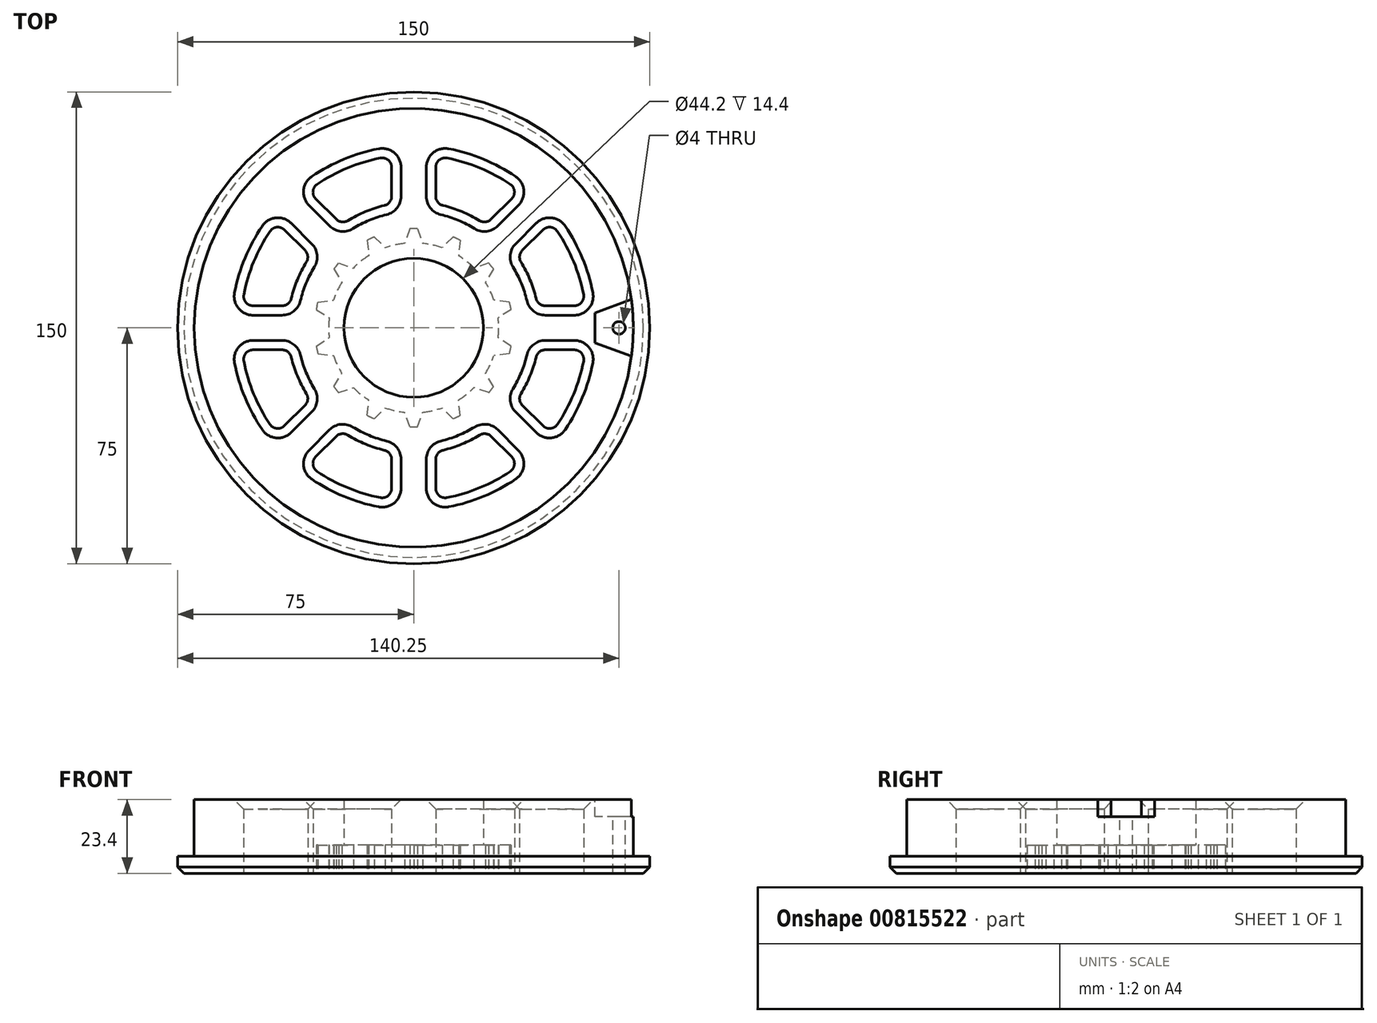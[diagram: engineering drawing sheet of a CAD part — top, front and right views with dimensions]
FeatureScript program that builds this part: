
annotation { "Feature Type Name" : "Feature", "Feature Type Description" : "" }
export const myFeature = defineFeature(function(context is Context, id is Id, definition is map)
    precondition{}
    {
        {
            var Q0;
            Q0=qCreatedBy(makeId("Top.planeOp"),FACE);
            var sketch = newSketch(context, id + "F0", { "sketchPlane" : qUnion([Q0])});
            skCircle(sketch, "E0", {"center": v(0, 0) * mm, "radius": 22.1 * mm});
            skCircle(sketch, "E1", {"center": v(0, 0) * mm, "radius": 75 * mm});
            skSolve(sketch);
        }
        {
            var Q0;
            Q0=qSketchRegion(id+"F0",true);
            extrude(context, id + "F1", {"entities" : qUnion([Q0]), "depth" : 23.4 * mm, "offsetDistance" : 25 * mm});
        }
        {
            var Q0;
            Q0=makeQuery(id+"F1.opExtrude","CAP_FACE",FACE,{"disambiguationData":[OSD([sQuery(id+"F0.wireOp",EDGE,"E0"),sQuery(id+"F0.wireOp",EDGE,"E1")])],"isStart":true});
            var sketch = newSketch(context, id + "F2", { "sketchPlane" : qUnion([Q0])});
            skCircle(sketch, "E2.0", {"center": v(0, 0) * mm, "radius": 22.1 * mm});
            skArc(sketch, "E3", {"start": v(2.9, -26.84) * mm, "mid": v(6, -26.32) * mm, "end": v(9.03, -25.44) * mm});
            skLineSegment(sketch, "E4", {"start": v(0, 0) * mm, "end": v(0, 59.3) * mm, "construction": true});
            skArc(sketch, "E5", {"start": v(0, -31.5) * mm, "mid": v(0.63, -31.5) * mm, "end": v(1.25, -31.48) * mm, "construction": true});
            skLineSegment(sketch, "E6", {"start": v(0, 31.5) * mm, "end": v(-1.25, 31.48) * mm});
            skLineSegment(sketch, "E7.MirrorCS", {"start": v(0, 31.5) * mm, "end": v(1.25, 31.48) * mm});
            skLineSegment(sketch, "E8", {"start": v(-1.25, 31.48) * mm, "end": v(-2.9, 26.84) * mm});
            skLineSegment(sketch, "E9", {"start": v(1.25, 31.48) * mm, "end": v(2.9, 26.84) * mm});
            skArc(sketch, "E10.1.0", {"start": v(0, -31.5) * mm, "mid": v(0.63, -31.5) * mm, "end": v(1.25, -31.48) * mm});
            skLineSegment(sketch, "E11.1.0", {"start": v(-12.53, 28.9) * mm, "end": v(-9.03, 25.44) * mm});
            skLineSegment(sketch, "E11.1.1", {"start": v(-14.78, 27.82) * mm, "end": v(-14.26, 22.93) * mm});
            skLineSegment(sketch, "E11.1.2", {"start": v(-13.67, 28.38) * mm, "end": v(-12.53, 28.9) * mm});
            skLineSegment(sketch, "E11.1.3", {"start": v(-13.67, 28.38) * mm, "end": v(-14.78, 27.82) * mm});
            skLineSegment(sketch, "E11.2.0", {"start": v(-23.83, 20.6) * mm, "end": v(-19.18, 19) * mm});
            skLineSegment(sketch, "E11.2.1", {"start": v(-25.39, 18.65) * mm, "end": v(-22.8, 14.47) * mm});
            skLineSegment(sketch, "E11.2.2", {"start": v(-24.63, 19.64) * mm, "end": v(-23.83, 20.6) * mm});
            skLineSegment(sketch, "E11.2.3", {"start": v(-24.63, 19.64) * mm, "end": v(-25.39, 18.65) * mm});
            skLineSegment(sketch, "E11.3.0", {"start": v(-30.4, 8.22) * mm, "end": v(-25.53, 8.8) * mm});
            skLineSegment(sketch, "E11.3.1", {"start": v(-30.96, 5.79) * mm, "end": v(-26.82, 3.15) * mm});
            skLineSegment(sketch, "E11.3.2", {"start": v(-30.71, 7) * mm, "end": v(-30.4, 8.22) * mm});
            skLineSegment(sketch, "E11.3.3", {"start": v(-30.71, 7) * mm, "end": v(-30.96, 5.79) * mm});
            skLineSegment(sketch, "E11.4.0", {"start": v(-30.96, -5.79) * mm, "end": v(-26.82, -3.15) * mm});
            skLineSegment(sketch, "E11.4.1", {"start": v(-30.4, -8.22) * mm, "end": v(-25.53, -8.8) * mm});
            skLineSegment(sketch, "E11.4.2", {"start": v(-30.71, -7) * mm, "end": v(-30.96, -5.79) * mm});
            skLineSegment(sketch, "E11.4.3", {"start": v(-30.71, -7) * mm, "end": v(-30.4, -8.22) * mm});
            skLineSegment(sketch, "E11.5.0", {"start": v(-25.39, -18.65) * mm, "end": v(-22.8, -14.47) * mm});
            skLineSegment(sketch, "E11.5.1", {"start": v(-23.83, -20.6) * mm, "end": v(-19.18, -19) * mm});
            skLineSegment(sketch, "E11.5.2", {"start": v(-24.63, -19.64) * mm, "end": v(-25.39, -18.65) * mm});
            skLineSegment(sketch, "E11.5.3", {"start": v(-24.63, -19.64) * mm, "end": v(-23.83, -20.6) * mm});
            skLineSegment(sketch, "E11.6.0", {"start": v(-14.78, -27.82) * mm, "end": v(-14.26, -22.93) * mm});
            skLineSegment(sketch, "E11.6.1", {"start": v(-12.53, -28.9) * mm, "end": v(-9.03, -25.44) * mm});
            skLineSegment(sketch, "E11.6.2", {"start": v(-13.67, -28.38) * mm, "end": v(-14.78, -27.82) * mm});
            skLineSegment(sketch, "E11.6.3", {"start": v(-13.67, -28.38) * mm, "end": v(-12.53, -28.9) * mm});
            skLineSegment(sketch, "E11.7.0", {"start": v(-1.25, -31.48) * mm, "end": v(-2.9, -26.84) * mm});
            skLineSegment(sketch, "E11.7.1", {"start": v(1.25, -31.48) * mm, "end": v(2.9, -26.84) * mm});
            skLineSegment(sketch, "E11.7.2", {"start": v(0, -31.5) * mm, "end": v(-1.25, -31.48) * mm});
            skLineSegment(sketch, "E11.7.3", {"start": v(0, -31.5) * mm, "end": v(1.25, -31.48) * mm});
            skLineSegment(sketch, "E11.8.0", {"start": v(12.53, -28.9) * mm, "end": v(9.03, -25.44) * mm});
            skLineSegment(sketch, "E11.8.1", {"start": v(14.78, -27.82) * mm, "end": v(14.26, -22.93) * mm});
            skLineSegment(sketch, "E11.8.2", {"start": v(13.67, -28.38) * mm, "end": v(12.53, -28.9) * mm});
            skLineSegment(sketch, "E11.8.3", {"start": v(13.67, -28.38) * mm, "end": v(14.78, -27.82) * mm});
            skLineSegment(sketch, "E11.9.0", {"start": v(23.83, -20.6) * mm, "end": v(19.18, -19) * mm});
            skLineSegment(sketch, "E11.9.1", {"start": v(25.39, -18.65) * mm, "end": v(22.8, -14.47) * mm});
            skLineSegment(sketch, "E11.9.2", {"start": v(24.63, -19.64) * mm, "end": v(23.83, -20.6) * mm});
            skLineSegment(sketch, "E11.9.3", {"start": v(24.63, -19.64) * mm, "end": v(25.39, -18.65) * mm});
            skLineSegment(sketch, "E11.10.0", {"start": v(30.4, -8.22) * mm, "end": v(25.53, -8.8) * mm});
            skLineSegment(sketch, "E11.10.1", {"start": v(30.96, -5.79) * mm, "end": v(26.82, -3.15) * mm});
            skLineSegment(sketch, "E11.10.2", {"start": v(30.71, -7) * mm, "end": v(30.4, -8.22) * mm});
            skLineSegment(sketch, "E11.10.3", {"start": v(30.71, -7) * mm, "end": v(30.96, -5.79) * mm});
            skLineSegment(sketch, "E11.11.0", {"start": v(30.96, 5.79) * mm, "end": v(26.82, 3.15) * mm});
            skLineSegment(sketch, "E11.11.1", {"start": v(30.4, 8.22) * mm, "end": v(25.53, 8.8) * mm});
            skLineSegment(sketch, "E11.11.2", {"start": v(30.71, 7) * mm, "end": v(30.96, 5.79) * mm});
            skLineSegment(sketch, "E11.11.3", {"start": v(30.71, 7) * mm, "end": v(30.4, 8.22) * mm});
            skLineSegment(sketch, "E11.12.0", {"start": v(25.39, 18.65) * mm, "end": v(22.8, 14.47) * mm});
            skLineSegment(sketch, "E11.12.1", {"start": v(23.83, 20.6) * mm, "end": v(19.18, 19) * mm});
            skLineSegment(sketch, "E11.12.2", {"start": v(24.63, 19.64) * mm, "end": v(25.39, 18.65) * mm});
            skLineSegment(sketch, "E11.12.3", {"start": v(24.63, 19.64) * mm, "end": v(23.83, 20.6) * mm});
            skLineSegment(sketch, "E11.13.0", {"start": v(14.78, 27.82) * mm, "end": v(14.26, 22.93) * mm});
            skLineSegment(sketch, "E11.13.1", {"start": v(12.53, 28.9) * mm, "end": v(9.03, 25.44) * mm});
            skLineSegment(sketch, "E11.13.2", {"start": v(13.67, 28.38) * mm, "end": v(14.78, 27.82) * mm});
            skLineSegment(sketch, "E11.13.3", {"start": v(13.67, 28.38) * mm, "end": v(12.53, 28.9) * mm});
            skArc(sketch, "E12.trimOffspring", {"start": v(-2.9, 26.84) * mm, "mid": v(-6, 26.32) * mm, "end": v(-9.03, 25.44) * mm, "construction": true});
            skPoint(sketch, "E13.start.orphan", {"position": v(0, 27) * mm});
            skArc(sketch, "E14.trimOffspring", {"start": v(-2.9, 26.84) * mm, "mid": v(-6, 26.32) * mm, "end": v(-9.03, 25.44) * mm});
            skArc(sketch, "E15.trimOffspring", {"start": v(-12.53, 28.9) * mm, "mid": v(-13.67, 28.38) * mm, "end": v(-14.78, 27.82) * mm, "construction": true});
            skArc(sketch, "E16.trimOffspring", {"start": v(-12.53, 28.9) * mm, "mid": v(-13.67, 28.38) * mm, "end": v(-14.78, 27.82) * mm});
            skArc(sketch, "E17.trimOffspring", {"start": v(1.25, 31.48) * mm, "mid": v(0, 31.5) * mm, "end": v(-1.25, 31.48) * mm, "construction": true});
            skArc(sketch, "E18.trimOffspring", {"start": v(1.25, 31.48) * mm, "mid": v(0, 31.5) * mm, "end": v(-1.25, 31.48) * mm});
            skArc(sketch, "E19.trimOffspring", {"start": v(9.03, 25.44) * mm, "mid": v(6, 26.32) * mm, "end": v(2.9, 26.84) * mm});
            skArc(sketch, "E20.trimOffspring", {"start": v(14.78, 27.82) * mm, "mid": v(13.67, 28.38) * mm, "end": v(12.53, 28.9) * mm, "construction": true});
            skArc(sketch, "E21.trimOffspring", {"start": v(14.78, 27.82) * mm, "mid": v(13.67, 28.38) * mm, "end": v(12.53, 28.9) * mm});
            skArc(sketch, "E22.trimOffspring", {"start": v(25.39, 18.65) * mm, "mid": v(24.63, 19.64) * mm, "end": v(23.83, 20.6) * mm, "construction": true});
            skArc(sketch, "E23.trimOffspring", {"start": v(19.18, 19) * mm, "mid": v(16.83, 21.1) * mm, "end": v(14.26, 22.93) * mm});
            skArc(sketch, "E24.trimOffspring", {"start": v(25.39, 18.65) * mm, "mid": v(24.63, 19.64) * mm, "end": v(23.83, 20.6) * mm});
            skArc(sketch, "E25.trimOffspring", {"start": v(25.53, 8.8) * mm, "mid": v(24.33, 11.71) * mm, "end": v(22.8, 14.47) * mm});
            skArc(sketch, "E26.trimOffspring", {"start": v(30.96, 5.79) * mm, "mid": v(30.71, 7) * mm, "end": v(30.4, 8.22) * mm, "construction": true});
            skArc(sketch, "E27.trimOffspring", {"start": v(30.96, 5.79) * mm, "mid": v(30.71, 7) * mm, "end": v(30.4, 8.22) * mm});
            skArc(sketch, "E28.trimOffspring", {"start": v(30.4, -8.22) * mm, "mid": v(30.71, -7) * mm, "end": v(30.96, -5.79) * mm, "construction": true});
            skArc(sketch, "E29.trimOffspring", {"start": v(30.4, -8.22) * mm, "mid": v(30.71, -7) * mm, "end": v(30.96, -5.79) * mm});
            skArc(sketch, "E30.trimOffspring", {"start": v(26.82, -3.15) * mm, "mid": v(27, 0) * mm, "end": v(26.82, 3.15) * mm});
            skArc(sketch, "E31.trimOffspring", {"start": v(22.8, -14.47) * mm, "mid": v(24.33, -11.71) * mm, "end": v(25.53, -8.8) * mm});
            skArc(sketch, "E32.trimOffspring", {"start": v(23.83, -20.6) * mm, "mid": v(24.63, -19.64) * mm, "end": v(25.39, -18.65) * mm, "construction": true});
            skArc(sketch, "E33.trimOffspring", {"start": v(23.83, -20.6) * mm, "mid": v(24.63, -19.64) * mm, "end": v(25.39, -18.65) * mm});
            skArc(sketch, "E34.trimOffspring", {"start": v(14.26, -22.93) * mm, "mid": v(16.83, -21.1) * mm, "end": v(19.18, -19) * mm});
            skArc(sketch, "E35.trimOffspring", {"start": v(12.53, -28.9) * mm, "mid": v(13.67, -28.38) * mm, "end": v(14.78, -27.82) * mm, "construction": true});
            skArc(sketch, "E36.trimOffspring", {"start": v(12.53, -28.9) * mm, "mid": v(13.67, -28.38) * mm, "end": v(14.78, -27.82) * mm});
            skPoint(sketch, "E37.orphan", {"position": v(0, -27) * mm});
            skArc(sketch, "E38.trimOffspring", {"start": v(-1.25, -31.48) * mm, "mid": v(-1.07, -31.48) * mm, "end": v(-0.88, -31.49) * mm, "construction": true});
            skArc(sketch, "E39.trimOffspring", {"start": v(-1.25, -31.48) * mm, "mid": v(-1.07, -31.48) * mm, "end": v(-0.88, -31.49) * mm});
            skArc(sketch, "E40.trimOffspring", {"start": v(-9.03, -25.44) * mm, "mid": v(-6, -26.32) * mm, "end": v(-2.9, -26.84) * mm, "construction": true});
            skArc(sketch, "E41.trimOffspring", {"start": v(-9.03, -25.44) * mm, "mid": v(-6, -26.32) * mm, "end": v(-2.9, -26.84) * mm});
            skArc(sketch, "E42.trimOffspring", {"start": v(-14.78, -27.82) * mm, "mid": v(-13.67, -28.38) * mm, "end": v(-12.53, -28.9) * mm, "construction": true});
            skArc(sketch, "E43.trimOffspring", {"start": v(-14.78, -27.82) * mm, "mid": v(-13.67, -28.38) * mm, "end": v(-12.53, -28.9) * mm});
            skArc(sketch, "E44.trimOffspring", {"start": v(-25.39, -18.65) * mm, "mid": v(-24.63, -19.64) * mm, "end": v(-23.83, -20.6) * mm, "construction": true});
            skArc(sketch, "E45.trimOffspring", {"start": v(-25.39, -18.65) * mm, "mid": v(-25.01, -19.15) * mm, "end": v(-24.63, -19.64) * mm});
            skArc(sketch, "E46.trimOffspring", {"start": v(-30.96, -5.79) * mm, "mid": v(-30.84, -6.4) * mm, "end": v(-30.71, -7) * mm, "construction": true});
            skArc(sketch, "E47.trimOffspring", {"start": v(-30.96, -5.79) * mm, "mid": v(-30.84, -6.4) * mm, "end": v(-30.71, -7) * mm});
            skArc(sketch, "E48.trimOffspring", {"start": v(-30.4, 8.22) * mm, "mid": v(-30.71, 7) * mm, "end": v(-30.96, 5.79) * mm, "construction": true});
            skArc(sketch, "E49.trimOffspring", {"start": v(-30.4, 8.22) * mm, "mid": v(-30.71, 7) * mm, "end": v(-30.96, 5.79) * mm});
            skArc(sketch, "E50.trimOffspring", {"start": v(-23.83, 20.6) * mm, "mid": v(-24.63, 19.64) * mm, "end": v(-25.39, 18.65) * mm, "construction": true});
            skArc(sketch, "E51.trimOffspring", {"start": v(-23.83, 20.6) * mm, "mid": v(-24.63, 19.64) * mm, "end": v(-25.39, 18.65) * mm});
            skArc(sketch, "E52.trimOffspring", {"start": v(-19.18, -19) * mm, "mid": v(-16.83, -21.1) * mm, "end": v(-14.26, -22.93) * mm});
            skArc(sketch, "E53.trimOffspring", {"start": v(-25.53, -8.8) * mm, "mid": v(-24.33, -11.71) * mm, "end": v(-22.8, -14.47) * mm});
            skArc(sketch, "E54.trimOffspring", {"start": v(-26.82, 3.15) * mm, "mid": v(-27, 0) * mm, "end": v(-26.82, -3.15) * mm});
            skArc(sketch, "E55.trimOffspring", {"start": v(-22.8, 14.47) * mm, "mid": v(-24.33, 11.71) * mm, "end": v(-25.53, 8.8) * mm, "construction": true});
            skArc(sketch, "E56.trimOffspring", {"start": v(-22.8, 14.47) * mm, "mid": v(-24.33, 11.71) * mm, "end": v(-25.53, 8.8) * mm});
            skArc(sketch, "E57.trimOffspring", {"start": v(-14.26, 22.93) * mm, "mid": v(-16.83, 21.1) * mm, "end": v(-19.18, 19) * mm, "construction": true});
            skArc(sketch, "E58.trimOffspring", {"start": v(-14.26, 22.93) * mm, "mid": v(-16.83, 21.1) * mm, "end": v(-19.18, 19) * mm});
            skSolve(sketch);
        }
        {
            var Q0;
            Q0=qSketchRegion(id+"F2",true);
            extrude(context, id + "F3", {"entities" : qUnion([Q0]), "operationType" : NewBodyOperationType.REMOVE, "oppositeDirection" : true, "depth" : 9 * mm, "offsetDistance" : 25 * mm});
        }
        {
            var Q0;
            Q0=makeQuery(id+"F1.opExtrude","CAP_FACE",FACE,{"disambiguationData":[OSD([sQuery(id+"F0.wireOp",EDGE,"E0"),sQuery(id+"F0.wireOp",EDGE,"E1")])],"isStart":true});
            var sketch = newSketch(context, id + "F4", { "sketchPlane" : qUnion([Q0])});
            skArc(sketch, "E59", {"start": v(-32.8, 22.9) * mm, "mid": v(-36.96, 15.3) * mm, "end": v(-39.38, 7) * mm});
            skArc(sketch, "E60", {"start": v(-43.53, 33.62) * mm, "mid": v(-50.81, 21.05) * mm, "end": v(-54.55, 7) * mm});
            skLineSegment(sketch, "E61", {"start": v(0, 0) * mm, "end": v(0, 117.13) * mm, "construction": true});
            skLineSegment(sketch, "E62", {"start": v(-7, 54.55) * mm, "end": v(-7, 39.38) * mm});
            skLineSegment(sketch, "E63.MirrorCS", {"start": v(7, 54.55) * mm, "end": v(7, 39.38) * mm});
            skLineSegment(sketch, "E64.1.0", {"start": v(-43.53, 33.62) * mm, "end": v(-32.8, 22.9) * mm});
            skLineSegment(sketch, "E64.1.1", {"start": v(-33.62, 43.53) * mm, "end": v(-22.9, 32.8) * mm});
            skLineSegment(sketch, "E64.2.0", {"start": v(-54.55, -7) * mm, "end": v(-39.38, -7) * mm});
            skLineSegment(sketch, "E64.2.1", {"start": v(-54.55, 7) * mm, "end": v(-39.38, 7) * mm});
            skLineSegment(sketch, "E64.3.0", {"start": v(-33.62, -43.53) * mm, "end": v(-22.9, -32.8) * mm});
            skLineSegment(sketch, "E64.3.1", {"start": v(-43.53, -33.62) * mm, "end": v(-32.8, -22.9) * mm});
            skLineSegment(sketch, "E64.4.0", {"start": v(7, -54.55) * mm, "end": v(7, -39.38) * mm});
            skLineSegment(sketch, "E64.4.1", {"start": v(-7, -54.55) * mm, "end": v(-7, -39.38) * mm});
            skLineSegment(sketch, "E64.5.0", {"start": v(43.53, -33.62) * mm, "end": v(32.8, -22.9) * mm});
            skLineSegment(sketch, "E64.5.1", {"start": v(33.62, -43.53) * mm, "end": v(22.9, -32.8) * mm});
            skLineSegment(sketch, "E64.6.0", {"start": v(54.55, 7) * mm, "end": v(39.38, 7) * mm});
            skLineSegment(sketch, "E64.6.1", {"start": v(54.55, -7) * mm, "end": v(39.38, -7) * mm});
            skLineSegment(sketch, "E64.7.0", {"start": v(33.62, 43.53) * mm, "end": v(22.9, 32.8) * mm});
            skLineSegment(sketch, "E64.7.1", {"start": v(43.53, 33.62) * mm, "end": v(32.8, 22.9) * mm});
            skArc(sketch, "E65.trimOffspring", {"start": v(-7, 39.38) * mm, "mid": v(-15.3, 36.96) * mm, "end": v(-22.9, 32.8) * mm});
            skArc(sketch, "E66.trimOffspring", {"start": v(-7, 54.55) * mm, "mid": v(-21.05, 50.81) * mm, "end": v(-33.62, 43.53) * mm});
            skArc(sketch, "E67.trimOffspring", {"start": v(33.62, 43.53) * mm, "mid": v(21.05, 50.81) * mm, "end": v(7, 54.55) * mm});
            skArc(sketch, "E68.trimOffspring", {"start": v(22.9, 32.8) * mm, "mid": v(15.3, 36.96) * mm, "end": v(7, 39.38) * mm});
            skArc(sketch, "E69.trimOffspring", {"start": v(39.38, 7) * mm, "mid": v(36.96, 15.3) * mm, "end": v(32.8, 22.9) * mm});
            skArc(sketch, "E70.trimOffspring", {"start": v(54.55, 7) * mm, "mid": v(50.81, 21.05) * mm, "end": v(43.53, 33.62) * mm});
            skArc(sketch, "E71.trimOffspring", {"start": v(43.53, -33.62) * mm, "mid": v(50.81, -21.05) * mm, "end": v(54.55, -7) * mm});
            skArc(sketch, "E72.trimOffspring", {"start": v(32.8, -22.9) * mm, "mid": v(36.96, -15.3) * mm, "end": v(39.38, -7) * mm});
            skArc(sketch, "E73.trimOffspring", {"start": v(7, -39.38) * mm, "mid": v(15.3, -36.96) * mm, "end": v(22.9, -32.8) * mm});
            skArc(sketch, "E74.trimOffspring", {"start": v(7, -54.55) * mm, "mid": v(21.05, -50.81) * mm, "end": v(33.62, -43.53) * mm});
            skArc(sketch, "E75.trimOffspring", {"start": v(-33.62, -43.53) * mm, "mid": v(-21.05, -50.81) * mm, "end": v(-7, -54.55) * mm});
            skArc(sketch, "E76.trimOffspring", {"start": v(-22.9, -32.8) * mm, "mid": v(-15.3, -36.96) * mm, "end": v(-7, -39.38) * mm});
            skArc(sketch, "E77.trimOffspring", {"start": v(-54.55, -7) * mm, "mid": v(-50.81, -21.05) * mm, "end": v(-43.53, -33.62) * mm});
            skArc(sketch, "E78.trimOffspring", {"start": v(-39.38, -7) * mm, "mid": v(-36.96, -15.3) * mm, "end": v(-32.8, -22.9) * mm});
            skSolve(sketch);
        }
        {
            var Q0;
            Q0=makeQuery(id+"F4.imprint","IMPRINT",FACE,{"disambiguationData":[TD([[makeQuery(id+"F4.imprint","IMPRINT",EDGE,{"derivedFrom":sQuery(id+"F4.wireOp",EDGE,"E59")}),-1.0]])]});
            var Q1;
            Q1=makeQuery(id+"F4.imprint","IMPRINT",FACE,{"disambiguationData":[TD([[makeQuery(id+"F4.imprint","IMPRINT",EDGE,{"derivedFrom":sQuery(id+"F4.wireOp",EDGE,"E62")}),-1.0]])]});
            var Q2;
            Q2=makeQuery(id+"F4.imprint","IMPRINT",FACE,{"disambiguationData":[TD([[makeQuery(id+"F4.imprint","IMPRINT",EDGE,{"derivedFrom":sQuery(id+"F4.wireOp",EDGE,"E63.MirrorCS")}),1.0]])]});
            var Q3;
            Q3=makeQuery(id+"F4.imprint","IMPRINT",FACE,{"disambiguationData":[TD([[makeQuery(id+"F4.imprint","IMPRINT",EDGE,{"derivedFrom":sQuery(id+"F4.wireOp",EDGE,"E64.6.0")}),-1.0]])]});
            var Q4;
            Q4=makeQuery(id+"F4.imprint","IMPRINT",FACE,{"disambiguationData":[TD([[makeQuery(id+"F4.imprint","IMPRINT",EDGE,{"derivedFrom":sQuery(id+"F4.wireOp",EDGE,"E64.5.0")}),-1.0]])]});
            var Q5;
            Q5=makeQuery(id+"F4.imprint","IMPRINT",FACE,{"disambiguationData":[TD([[makeQuery(id+"F4.imprint","IMPRINT",EDGE,{"derivedFrom":sQuery(id+"F4.wireOp",EDGE,"E64.4.0")}),-1.0]])]});
            var Q6;
            Q6=makeQuery(id+"F4.imprint","IMPRINT",FACE,{"disambiguationData":[TD([[makeQuery(id+"F4.imprint","IMPRINT",EDGE,{"derivedFrom":sQuery(id+"F4.wireOp",EDGE,"E64.3.0")}),-1.0]])]});
            var Q7;
            Q7=makeQuery(id+"F4.imprint","IMPRINT",FACE,{"disambiguationData":[TD([[makeQuery(id+"F4.imprint","IMPRINT",EDGE,{"derivedFrom":sQuery(id+"F4.wireOp",EDGE,"E64.2.0")}),-1.0]])]});
            extrude(context, id + "F5", {"entities" : qUnion([Q0, Q1, Q2, Q3, Q4, Q5, Q6, Q7]), "operationType" : NewBodyOperationType.REMOVE, "oppositeDirection" : true, "depth" : 25 * mm, "offsetDistance" : 25 * mm});
        }
        {
            var Q0;
            Q0=makeQuery(id+"F1.opExtrude","CAP_FACE",FACE,{"disambiguationData":[OSD([sQuery(id+"F0.wireOp",EDGE,"E0"),sQuery(id+"F0.wireOp",EDGE,"E1")])],"isStart":false});
            var sketch = newSketch(context, id + "F6", { "sketchPlane" : qUnion([Q0])});
            skCircle(sketch, "E79", {"center": v(0, 0) * mm, "radius": 69.75 * mm});
            skCircle(sketch, "E80.0", {"center": v(0, 0) * mm, "radius": 75 * mm});
            skSolve(sketch);
        }
        {
            var Q0;
            Q0 = qSketchRegion(id + "F6", true);
            extrude(context, id + "F7", {"entities" : qUnion([Q0]), "operationType" : NewBodyOperationType.REMOVE, "oppositeDirection" : true, "depth" : 18 * mm, "offsetDistance" : 25 * mm});
        }
        {
            var Q0;
            Q0=makeQuery(id+"F1.opExtrude","CAP_FACE",FACE,{"disambiguationData":[OSD([sQuery(id+"F0.wireOp",EDGE,"E0"),sQuery(id+"F0.wireOp",EDGE,"E1")])],"isStart":false});
            var sketch = newSketch(context, id + "F8", { "sketchPlane" : qUnion([Q0])});
            skLineSegment(sketch, "E81", {"start": v(0, 0) * mm, "end": v(90.37, 0) * mm, "construction": true});
            skArc(sketch, "E82.0", {"start": v(69.17, -9) * mm, "mid": v(69.75, 0) * mm, "end": v(69.17, 9) * mm});
            skLineSegment(sketch, "E83", {"start": v(69.17, 9) * mm, "end": v(57.6, 4.8) * mm});
            skLineSegment(sketch, "E84", {"start": v(57.6, 4.8) * mm, "end": v(57.6, 0) * mm});
            skLineSegment(sketch, "E85.MirrorCS", {"start": v(57.6, -4.8) * mm, "end": v(57.6, 0) * mm});
            skLineSegment(sketch, "E86.MirrorCS", {"start": v(69.17, -9) * mm, "end": v(57.6, -4.8) * mm});
            skSolve(sketch);
        }
        {
            var Q0;
            Q0 = qSketchRegion(id + "F8", true);
            extrude(context, id + "F9", {"entities" : qUnion([Q0]), "operationType" : NewBodyOperationType.REMOVE, "oppositeDirection" : true, "depth" : 5.4 * mm, "offsetDistance" : 25 * mm});
        }
        {
            var Q0;
            Q0=makeQuery(id+"F9.boolean.opBoolean","COPY",FACE,{"derivedFrom":makeQuery(id+"F9.opExtrude","CAP_FACE",FACE,{"disambiguationData":[OSD([sQuery(id+"F8.wireOp",EDGE,"E82.0"),sQuery(id+"F8.wireOp",EDGE,"E83"),sQuery(id+"F8.wireOp",EDGE,"E84"),sQuery(id+"F8.wireOp",EDGE,"E85.MirrorCS"),sQuery(id+"F8.wireOp",EDGE,"E86.MirrorCS")])],"isStart":false})});
            var sketch = newSketch(context, id + "F10", { "sketchPlane" : qUnion([Q0])});
            skLineSegment(sketch, "E87", {"start": v(87.26, 0) * mm, "end": v(136.23, 0) * mm, "construction": true});
            skCircle(sketch, "E88", {"center": v(65.25, 0) * mm, "radius": 2 * mm});
            skPoint(sketch, "E89", {"position": v(57.6, 0) * mm});
            skSolve(sketch);
        }
        {
            var Q0;
            Q0=makeQuery(id+"F10.imprint","IMPRINT",FACE,{"disambiguationData":[TD([[makeQuery(id+"F10.imprint","IMPRINT",EDGE,{"derivedFrom":sQuery(id+"F10.wireOp",EDGE,"E88")}),1.0]])]});
            var Q1;
            Q1=sQuery(id+"F10.wireOp",EDGE,"E88");
            extrude(context, id + "F11", {"entities" : qUnion([Q0]), "operationType" : NewBodyOperationType.REMOVE, "surfaceEntities" : qUnion([Q1]), "oppositeDirection" : true, "depth" : 25 * mm, "offsetDistance" : 25 * mm});
        }
        {
            var Q0;
            Q0=makeQuery(id+"F5.boolean.opBoolean","COPY",EDGE,{"derivedFrom":makeQuery(id+"F5.opExtrude","SWEPT_EDGE",EDGE,{"disambiguationData":[OSD([sQuery(id+"F4.wireOp",EDGE,"E64.6.0"),sQuery(id+"F4.wireOp",EDGE,"E70.trimOffspring")])]})});
            var Q1;
            Q1=makeQuery(id+"F5.boolean.opBoolean","COPY",EDGE,{"derivedFrom":makeQuery(id+"F5.opExtrude","SWEPT_EDGE",EDGE,{"disambiguationData":[OSD([sQuery(id+"F4.wireOp",EDGE,"E64.7.1"),sQuery(id+"F4.wireOp",EDGE,"E70.trimOffspring")])]})});
            var Q2;
            Q2=makeQuery(id+"F5.boolean.opBoolean","COPY",EDGE,{"derivedFrom":makeQuery(id+"F5.opExtrude","SWEPT_EDGE",EDGE,{"disambiguationData":[OSD([sQuery(id+"F4.wireOp",EDGE,"E64.6.0"),sQuery(id+"F4.wireOp",EDGE,"E69.trimOffspring")])]})});
            var Q3;
            Q3=makeQuery(id+"F5.boolean.opBoolean","COPY",EDGE,{"derivedFrom":makeQuery(id+"F5.opExtrude","SWEPT_EDGE",EDGE,{"disambiguationData":[OSD([sQuery(id+"F4.wireOp",EDGE,"E64.7.1"),sQuery(id+"F4.wireOp",EDGE,"E69.trimOffspring")])]})});
            var Q4;
            Q4=makeQuery(id+"F5.boolean.opBoolean","COPY",EDGE,{"derivedFrom":makeQuery(id+"F5.opExtrude","SWEPT_EDGE",EDGE,{"disambiguationData":[OSD([sQuery(id+"F4.wireOp",EDGE,"E64.6.1"),sQuery(id+"F4.wireOp",EDGE,"E71.trimOffspring")])]})});
            var Q5;
            Q5=makeQuery(id+"F5.boolean.opBoolean","COPY",EDGE,{"derivedFrom":makeQuery(id+"F5.opExtrude","SWEPT_EDGE",EDGE,{"disambiguationData":[OSD([sQuery(id+"F4.wireOp",EDGE,"E64.6.1"),sQuery(id+"F4.wireOp",EDGE,"E72.trimOffspring")])]})});
            var Q6;
            Q6=makeQuery(id+"F5.boolean.opBoolean","COPY",EDGE,{"derivedFrom":makeQuery(id+"F5.opExtrude","SWEPT_EDGE",EDGE,{"disambiguationData":[OSD([sQuery(id+"F4.wireOp",EDGE,"E64.5.0"),sQuery(id+"F4.wireOp",EDGE,"E72.trimOffspring")])]})});
            var Q7;
            Q7=makeQuery(id+"F5.boolean.opBoolean","COPY",EDGE,{"derivedFrom":makeQuery(id+"F5.opExtrude","SWEPT_EDGE",EDGE,{"disambiguationData":[OSD([sQuery(id+"F4.wireOp",EDGE,"E64.5.0"),sQuery(id+"F4.wireOp",EDGE,"E71.trimOffspring")])]})});
            var Q8;
            Q8=makeQuery(id+"F5.boolean.opBoolean","COPY",EDGE,{"derivedFrom":makeQuery(id+"F5.opExtrude","SWEPT_EDGE",EDGE,{"disambiguationData":[OSD([sQuery(id+"F4.wireOp",EDGE,"E64.7.0"),sQuery(id+"F4.wireOp",EDGE,"E67.trimOffspring")])]})});
            var Q9;
            Q9=makeQuery(id+"F5.boolean.opBoolean","COPY",EDGE,{"derivedFrom":makeQuery(id+"F5.opExtrude","SWEPT_EDGE",EDGE,{"disambiguationData":[OSD([sQuery(id+"F4.wireOp",EDGE,"E64.7.0"),sQuery(id+"F4.wireOp",EDGE,"E68.trimOffspring")])]})});
            var Q10;
            Q10=makeQuery(id+"F5.boolean.opBoolean","COPY",EDGE,{"derivedFrom":makeQuery(id+"F5.opExtrude","SWEPT_EDGE",EDGE,{"disambiguationData":[OSD([sQuery(id+"F4.wireOp",EDGE,"E63.MirrorCS"),sQuery(id+"F4.wireOp",EDGE,"E67.trimOffspring")])]})});
            var Q11;
            Q11=makeQuery(id+"F5.boolean.opBoolean","COPY",EDGE,{"derivedFrom":makeQuery(id+"F5.opExtrude","SWEPT_EDGE",EDGE,{"disambiguationData":[OSD([sQuery(id+"F4.wireOp",EDGE,"E63.MirrorCS"),sQuery(id+"F4.wireOp",EDGE,"E68.trimOffspring")])]})});
            var Q12;
            Q12=makeQuery(id+"F5.boolean.opBoolean","COPY",EDGE,{"derivedFrom":makeQuery(id+"F5.opExtrude","SWEPT_EDGE",EDGE,{"disambiguationData":[OSD([sQuery(id+"F4.wireOp",EDGE,"E62"),sQuery(id+"F4.wireOp",EDGE,"E66.trimOffspring")])]})});
            var Q13;
            Q13=makeQuery(id+"F5.boolean.opBoolean","COPY",EDGE,{"derivedFrom":makeQuery(id+"F5.opExtrude","SWEPT_EDGE",EDGE,{"disambiguationData":[OSD([sQuery(id+"F4.wireOp",EDGE,"E62"),sQuery(id+"F4.wireOp",EDGE,"E65.trimOffspring")])]})});
            var Q14;
            Q14=makeQuery(id+"F5.boolean.opBoolean","COPY",EDGE,{"derivedFrom":makeQuery(id+"F5.opExtrude","SWEPT_EDGE",EDGE,{"disambiguationData":[OSD([sQuery(id+"F4.wireOp",EDGE,"E64.1.1"),sQuery(id+"F4.wireOp",EDGE,"E66.trimOffspring")])]})});
            var Q15;
            Q15=makeQuery(id+"F5.boolean.opBoolean","COPY",EDGE,{"derivedFrom":makeQuery(id+"F5.opExtrude","SWEPT_EDGE",EDGE,{"disambiguationData":[OSD([sQuery(id+"F4.wireOp",EDGE,"E64.1.1"),sQuery(id+"F4.wireOp",EDGE,"E65.trimOffspring")])]})});
            var Q16;
            Q16=makeQuery(id+"F5.boolean.opBoolean","COPY",EDGE,{"derivedFrom":makeQuery(id+"F5.opExtrude","SWEPT_EDGE",EDGE,{"disambiguationData":[OSD([sQuery(id+"F4.wireOp",EDGE,"E60"),sQuery(id+"F4.wireOp",EDGE,"E64.2.1")])]})});
            var Q17;
            Q17=makeQuery(id+"F5.boolean.opBoolean","COPY",EDGE,{"derivedFrom":makeQuery(id+"F5.opExtrude","SWEPT_EDGE",EDGE,{"disambiguationData":[OSD([sQuery(id+"F4.wireOp",EDGE,"E64.3.1"),sQuery(id+"F4.wireOp",EDGE,"E77.trimOffspring")])]})});
            var Q18;
            Q18=makeQuery(id+"F5.boolean.opBoolean","COPY",EDGE,{"derivedFrom":makeQuery(id+"F5.opExtrude","SWEPT_EDGE",EDGE,{"disambiguationData":[OSD([sQuery(id+"F4.wireOp",EDGE,"E64.2.0"),sQuery(id+"F4.wireOp",EDGE,"E77.trimOffspring")])]})});
            var Q19;
            Q19=makeQuery(id+"F5.boolean.opBoolean","COPY",EDGE,{"derivedFrom":makeQuery(id+"F5.opExtrude","SWEPT_EDGE",EDGE,{"disambiguationData":[OSD([sQuery(id+"F4.wireOp",EDGE,"E60"),sQuery(id+"F4.wireOp",EDGE,"E64.1.0")])]})});
            var Q20;
            Q20=makeQuery(id+"F5.boolean.opBoolean","COPY",EDGE,{"derivedFrom":makeQuery(id+"F5.opExtrude","SWEPT_EDGE",EDGE,{"disambiguationData":[OSD([sQuery(id+"F4.wireOp",EDGE,"E59"),sQuery(id+"F4.wireOp",EDGE,"E64.1.0")])]})});
            var Q21;
            Q21=makeQuery(id+"F5.boolean.opBoolean","COPY",EDGE,{"derivedFrom":makeQuery(id+"F5.opExtrude","SWEPT_EDGE",EDGE,{"disambiguationData":[OSD([sQuery(id+"F4.wireOp",EDGE,"E59"),sQuery(id+"F4.wireOp",EDGE,"E64.2.1")])]})});
            var Q22;
            Q22=makeQuery(id+"F5.boolean.opBoolean","COPY",EDGE,{"derivedFrom":makeQuery(id+"F5.opExtrude","SWEPT_EDGE",EDGE,{"disambiguationData":[OSD([sQuery(id+"F4.wireOp",EDGE,"E64.3.1"),sQuery(id+"F4.wireOp",EDGE,"E78.trimOffspring")])]})});
            var Q23;
            Q23=makeQuery(id+"F5.boolean.opBoolean","COPY",EDGE,{"derivedFrom":makeQuery(id+"F5.opExtrude","SWEPT_EDGE",EDGE,{"disambiguationData":[OSD([sQuery(id+"F4.wireOp",EDGE,"E64.2.0"),sQuery(id+"F4.wireOp",EDGE,"E78.trimOffspring")])]})});
            var Q24;
            Q24=makeQuery(id+"F5.boolean.opBoolean","COPY",EDGE,{"derivedFrom":makeQuery(id+"F5.opExtrude","SWEPT_EDGE",EDGE,{"disambiguationData":[OSD([sQuery(id+"F4.wireOp",EDGE,"E64.4.1"),sQuery(id+"F4.wireOp",EDGE,"E76.trimOffspring")])]})});
            var Q25;
            Q25=makeQuery(id+"F5.boolean.opBoolean","COPY",EDGE,{"derivedFrom":makeQuery(id+"F5.opExtrude","SWEPT_EDGE",EDGE,{"disambiguationData":[OSD([sQuery(id+"F4.wireOp",EDGE,"E64.3.0"),sQuery(id+"F4.wireOp",EDGE,"E76.trimOffspring")])]})});
            var Q26;
            Q26=makeQuery(id+"F5.boolean.opBoolean","COPY",EDGE,{"derivedFrom":makeQuery(id+"F5.opExtrude","SWEPT_EDGE",EDGE,{"disambiguationData":[OSD([sQuery(id+"F4.wireOp",EDGE,"E64.4.1"),sQuery(id+"F4.wireOp",EDGE,"E75.trimOffspring")])]})});
            var Q27;
            Q27=makeQuery(id+"F5.boolean.opBoolean","COPY",EDGE,{"derivedFrom":makeQuery(id+"F5.opExtrude","SWEPT_EDGE",EDGE,{"disambiguationData":[OSD([sQuery(id+"F4.wireOp",EDGE,"E64.3.0"),sQuery(id+"F4.wireOp",EDGE,"E75.trimOffspring")])]})});
            var Q28;
            Q28=makeQuery(id+"F5.boolean.opBoolean","COPY",EDGE,{"derivedFrom":makeQuery(id+"F5.opExtrude","SWEPT_EDGE",EDGE,{"disambiguationData":[OSD([sQuery(id+"F4.wireOp",EDGE,"E64.4.0"),sQuery(id+"F4.wireOp",EDGE,"E74.trimOffspring")])]})});
            var Q29;
            Q29=makeQuery(id+"F5.boolean.opBoolean","COPY",EDGE,{"derivedFrom":makeQuery(id+"F5.opExtrude","SWEPT_EDGE",EDGE,{"disambiguationData":[OSD([sQuery(id+"F4.wireOp",EDGE,"E64.5.1"),sQuery(id+"F4.wireOp",EDGE,"E73.trimOffspring")])]})});
            var Q30;
            Q30=makeQuery(id+"F5.boolean.opBoolean","COPY",EDGE,{"derivedFrom":makeQuery(id+"F5.opExtrude","SWEPT_EDGE",EDGE,{"disambiguationData":[OSD([sQuery(id+"F4.wireOp",EDGE,"E64.5.1"),sQuery(id+"F4.wireOp",EDGE,"E74.trimOffspring")])]})});
            var Q31;
            Q31=makeQuery(id+"F5.boolean.opBoolean","COPY",EDGE,{"derivedFrom":makeQuery(id+"F5.opExtrude","SWEPT_EDGE",EDGE,{"disambiguationData":[OSD([sQuery(id+"F4.wireOp",EDGE,"E64.4.0"),sQuery(id+"F4.wireOp",EDGE,"E73.trimOffspring")])]})});
            fillet(context, id + "F12", {"entities" : qUnion([Q0, Q1, Q2, Q3, Q4, Q5, Q6, Q7, Q8, Q9, Q10, Q11, Q12, Q13, Q14, Q15, Q16, Q17, Q18, Q19, Q20, Q21, Q22, Q23, Q24, Q25, Q26, Q27, Q28, Q29, Q30, Q31]), "radius" : 3 * mm, "tangentPropagation" : true, "allowEdgeOverflow" : false});
        }
        {
            var Q0;
            Q0=makeQuery(id+"F5.boolean.opBoolean","INTERSECT",EDGE,{"derivedFrom":[makeQuery(id+"F1.opExtrude","CAP_FACE",FACE,{"disambiguationData":[OSD([sQuery(id+"F0.wireOp",EDGE,"E0"),sQuery(id+"F0.wireOp",EDGE,"E1")])],"isStart":false}),makeQuery(id+"F5.opExtrude","SWEPT_FACE",FACE,{"disambiguationData":[OSD([sQuery(id+"F4.wireOp",EDGE,"E70.trimOffspring")])]})]});
            var Q1;
            Q1=makeQuery(id+"F5.boolean.opBoolean","INTERSECT",EDGE,{"derivedFrom":[makeQuery(id+"F1.opExtrude","CAP_FACE",FACE,{"disambiguationData":[OSD([sQuery(id+"F0.wireOp",EDGE,"E0"),sQuery(id+"F0.wireOp",EDGE,"E1")])],"isStart":false}),makeQuery(id+"F5.opExtrude","SWEPT_FACE",FACE,{"disambiguationData":[OSD([sQuery(id+"F4.wireOp",EDGE,"E71.trimOffspring")])]})]});
            var Q2;
            Q2=makeQuery(id+"F5.boolean.opBoolean","INTERSECT",EDGE,{"derivedFrom":[makeQuery(id+"F1.opExtrude","CAP_FACE",FACE,{"disambiguationData":[OSD([sQuery(id+"F0.wireOp",EDGE,"E0"),sQuery(id+"F0.wireOp",EDGE,"E1")])],"isStart":false}),makeQuery(id+"F5.opExtrude","SWEPT_FACE",FACE,{"disambiguationData":[OSD([sQuery(id+"F4.wireOp",EDGE,"E73.trimOffspring")])]})]});
            var Q3;
            Q3=makeQuery(id+"F5.boolean.opBoolean","INTERSECT",EDGE,{"derivedFrom":[makeQuery(id+"F1.opExtrude","CAP_FACE",FACE,{"disambiguationData":[OSD([sQuery(id+"F0.wireOp",EDGE,"E0"),sQuery(id+"F0.wireOp",EDGE,"E1")])],"isStart":false}),makeQuery(id+"F5.opExtrude","SWEPT_FACE",FACE,{"disambiguationData":[OSD([sQuery(id+"F4.wireOp",EDGE,"E76.trimOffspring")])]})]});
            var Q4;
            Q4=makeQuery(id+"F5.boolean.opBoolean","INTERSECT",EDGE,{"derivedFrom":[makeQuery(id+"F1.opExtrude","CAP_FACE",FACE,{"disambiguationData":[OSD([sQuery(id+"F0.wireOp",EDGE,"E0"),sQuery(id+"F0.wireOp",EDGE,"E1")])],"isStart":false}),makeQuery(id+"F5.opExtrude","SWEPT_FACE",FACE,{"disambiguationData":[OSD([sQuery(id+"F4.wireOp",EDGE,"E78.trimOffspring")])]})]});
            var Q5;
            Q5=makeQuery(id+"F5.boolean.opBoolean","INTERSECT",EDGE,{"derivedFrom":[makeQuery(id+"F1.opExtrude","CAP_FACE",FACE,{"disambiguationData":[OSD([sQuery(id+"F0.wireOp",EDGE,"E0"),sQuery(id+"F0.wireOp",EDGE,"E1")])],"isStart":false}),makeQuery(id+"F5.opExtrude","SWEPT_FACE",FACE,{"disambiguationData":[OSD([sQuery(id+"F4.wireOp",EDGE,"E59")])]})]});
            var Q6;
            Q6=makeQuery(id+"F5.boolean.opBoolean","INTERSECT",EDGE,{"derivedFrom":[makeQuery(id+"F1.opExtrude","CAP_FACE",FACE,{"disambiguationData":[OSD([sQuery(id+"F0.wireOp",EDGE,"E0"),sQuery(id+"F0.wireOp",EDGE,"E1")])],"isStart":false}),makeQuery(id+"F5.opExtrude","SWEPT_FACE",FACE,{"disambiguationData":[OSD([sQuery(id+"F4.wireOp",EDGE,"E65.trimOffspring")])]})]});
            var Q7;
            Q7=makeQuery(id+"F5.boolean.opBoolean","INTERSECT",EDGE,{"derivedFrom":[makeQuery(id+"F1.opExtrude","CAP_FACE",FACE,{"disambiguationData":[OSD([sQuery(id+"F0.wireOp",EDGE,"E0"),sQuery(id+"F0.wireOp",EDGE,"E1")])],"isStart":false}),makeQuery(id+"F5.opExtrude","SWEPT_FACE",FACE,{"disambiguationData":[OSD([sQuery(id+"F4.wireOp",EDGE,"E68.trimOffspring")])]})]});
            var Q8;
            Q8=makeQuery(id+"F5.boolean.opBoolean","COPY",EDGE,{"derivedFrom":makeQuery(id+"F5.opExtrude","CAP_EDGE",EDGE,{"disambiguationData":[OSD([sQuery(id+"F4.wireOp",EDGE,"E70.trimOffspring")])],"isStart":true})});
            var Q9;
            Q9=makeQuery(id+"F5.boolean.opBoolean","COPY",EDGE,{"derivedFrom":makeQuery(id+"F5.opExtrude","CAP_EDGE",EDGE,{"disambiguationData":[OSD([sQuery(id+"F4.wireOp",EDGE,"E71.trimOffspring")])],"isStart":true})});
            var Q10;
            Q10=makeQuery(id+"F5.boolean.opBoolean","COPY",EDGE,{"derivedFrom":makeQuery(id+"F5.opExtrude","CAP_EDGE",EDGE,{"disambiguationData":[OSD([sQuery(id+"F4.wireOp",EDGE,"E74.trimOffspring")])],"isStart":true})});
            var Q11;
            Q11=makeQuery(id+"F5.boolean.opBoolean","COPY",EDGE,{"derivedFrom":makeQuery(id+"F5.opExtrude","CAP_EDGE",EDGE,{"disambiguationData":[OSD([sQuery(id+"F4.wireOp",EDGE,"E75.trimOffspring")])],"isStart":true})});
            var Q12;
            Q12=makeQuery(id+"F5.boolean.opBoolean","COPY",EDGE,{"derivedFrom":makeQuery(id+"F5.opExtrude","CAP_EDGE",EDGE,{"disambiguationData":[OSD([sQuery(id+"F4.wireOp",EDGE,"E77.trimOffspring")])],"isStart":true})});
            var Q13;
            Q13=makeQuery(id+"F5.boolean.opBoolean","COPY",EDGE,{"derivedFrom":makeQuery(id+"F5.opExtrude","CAP_EDGE",EDGE,{"disambiguationData":[OSD([sQuery(id+"F4.wireOp",EDGE,"E60")])],"isStart":true})});
            var Q14;
            Q14=makeQuery(id+"F5.boolean.opBoolean","COPY",EDGE,{"derivedFrom":makeQuery(id+"F5.opExtrude","CAP_EDGE",EDGE,{"disambiguationData":[OSD([sQuery(id+"F4.wireOp",EDGE,"E66.trimOffspring")])],"isStart":true})});
            var Q15;
            Q15=makeQuery(id+"F5.boolean.opBoolean","COPY",EDGE,{"derivedFrom":makeQuery(id+"F5.opExtrude","CAP_EDGE",EDGE,{"disambiguationData":[OSD([sQuery(id+"F4.wireOp",EDGE,"E67.trimOffspring")])],"isStart":true})});
            chamfer(context, id + "F13", {"entities" : qUnion([Q0, Q1, Q2, Q3, Q4, Q5, Q6, Q7, Q8, Q9, Q10, Q11, Q12, Q13, Q14, Q15]), "width" : 3 * mm, "tangentPropagation" : true});
        }
        {
            var Q0;
            Q0=makeQuery(id+"F1.opExtrude","CAP_EDGE",EDGE,{"disambiguationData":[OSD([sQuery(id+"F0.wireOp",EDGE,"E1")])],"isStart":true});
            chamfer(context, id + "F14", {"entities" : qUnion([Q0]), "width" : 2 * mm, "tangentPropagation" : true});
        }
    });
